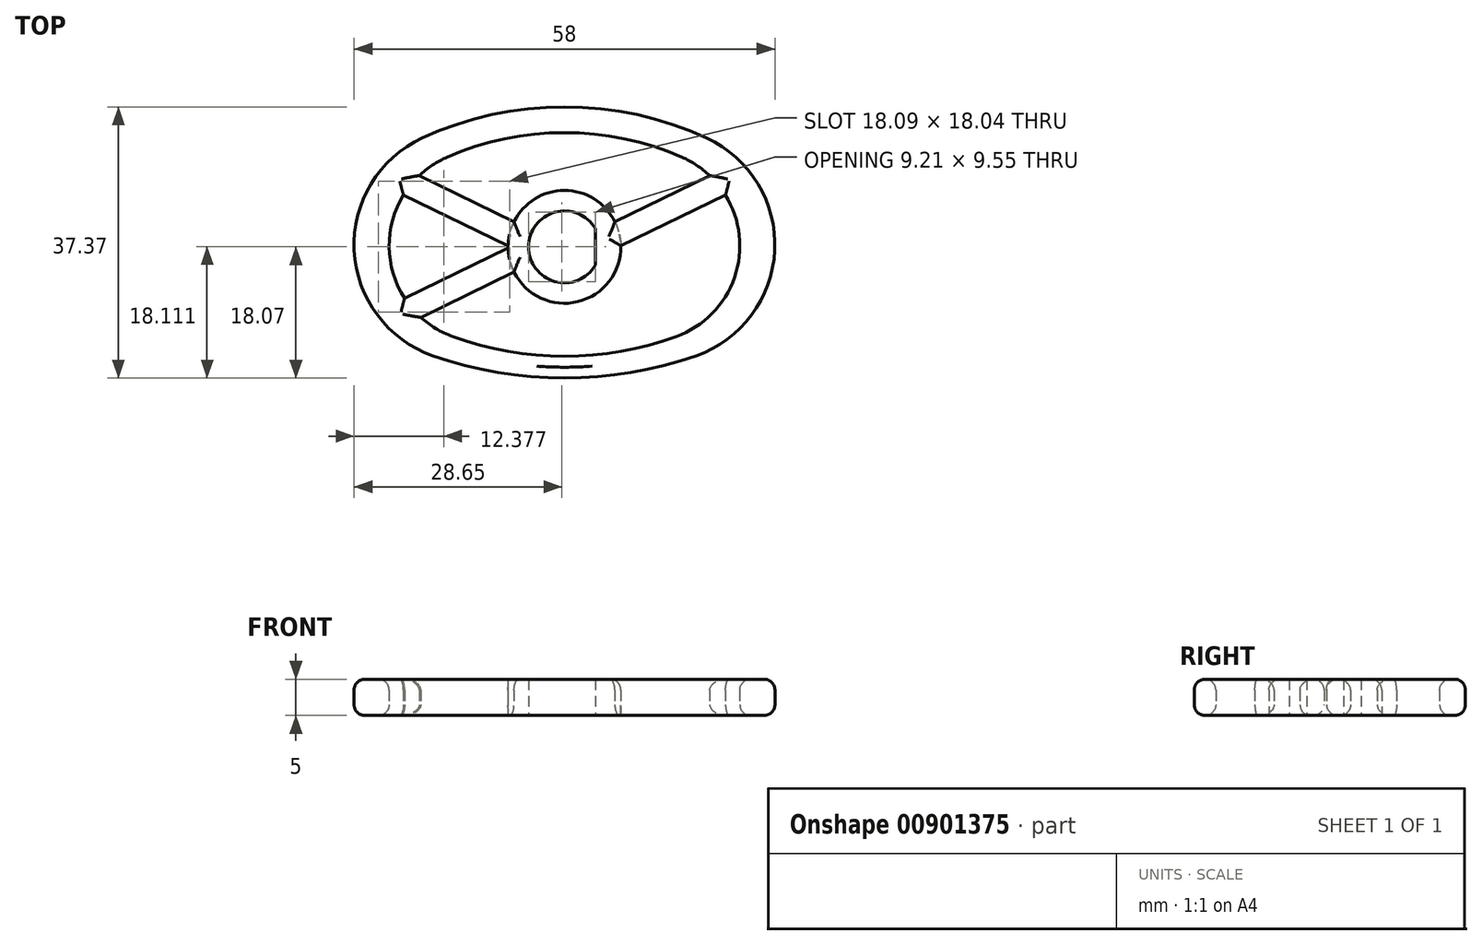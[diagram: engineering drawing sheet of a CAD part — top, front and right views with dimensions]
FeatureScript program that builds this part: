
annotation { "Feature Type Name" : "Feature", "Feature Type Description" : "" }
export const myFeature = defineFeature(function(context is Context, id is Id, definition is map)
    precondition{}
    {
        {
            var Q0;
            Q0=qCreatedBy(makeId("Top.planeOp"),FACE);
            var sketch = newSketch(context, id + "F0", { "sketchPlane" : qUnion([Q0])});
            skArc(sketch, "E0", {"start": v(4.25, 2.54) * mm, "mid": v(-4.95, 0) * mm, "end": v(4.25, -2.54) * mm});
            skLineSegment(sketch, "E1", {"start": v(4.25, 2.54) * mm, "end": v(4.25, -2.54) * mm});
            skArc(sketch, "E2", {"start": v(-19.59, 15) * mm, "mid": v(-28.98, -0.49) * mm, "end": v(-18.14, -15) * mm});
            skArc(sketch, "E3.MirrorCS", {"start": v(19.59, 15) * mm, "mid": v(28.98, -0.49) * mm, "end": v(18.14, -15) * mm});
            skArc(sketch, "E4", {"start": v(19.59, 15) * mm, "mid": v(0, 19.3) * mm, "end": v(-19.59, 15) * mm});
            skArc(sketch, "E5", {"start": v(-18.14, -15) * mm, "mid": v(0, -18.07) * mm, "end": v(18.14, -15) * mm});
            skArc(sketch, "E6", {"start": v(-16.17, 12.37) * mm, "mid": v(-24.16, -0.26) * mm, "end": v(-15.41, -12.37) * mm});
            skArc(sketch, "E7.MirrorCS", {"start": v(16.17, 12.37) * mm, "mid": v(24.16, -0.26) * mm, "end": v(15.41, -12.37) * mm});
            skArc(sketch, "E8", {"start": v(16.17, 12.37) * mm, "mid": v(0, 15.74) * mm, "end": v(-16.17, 12.37) * mm});
            skArc(sketch, "E9", {"start": v(-15.41, -12.37) * mm, "mid": v(0, -15.1) * mm, "end": v(15.41, -12.37) * mm});
            skCircle(sketch, "E10", {"center": v(0, 0) * mm, "radius": 7.77 * mm});
            skLineSegment(sketch, "E11", {"start": v(-7.77, 0.15) * mm, "end": v(-22.19, 7.15) * mm});
            skLineSegment(sketch, "E12", {"start": v(-6.95, 3.49) * mm, "end": v(-20.01, 9.83) * mm});
            skLineSegment(sketch, "E13.MirrorCS", {"start": v(6.95, 3.49) * mm, "end": v(20.01, 9.83) * mm});
            skLineSegment(sketch, "E14.MirrorCS", {"start": v(7.77, 0.15) * mm, "end": v(22.19, 7.15) * mm});
            skLineSegment(sketch, "E15.MirrorCS", {"start": v(-7.77, -0.15) * mm, "end": v(-22.19, -7.15) * mm});
            skLineSegment(sketch, "E16.MirrorCS", {"start": v(-6.95, -3.49) * mm, "end": v(-20.01, -9.83) * mm});
            skLineSegment(sketch, "E17.MirrorCS", {"start": v(7.77, -0.15) * mm, "end": v(22.19, -7.15) * mm});
            skLineSegment(sketch, "E18.MirrorCS", {"start": v(6.95, -3.49) * mm, "end": v(20.01, -9.83) * mm});
            skSolve(sketch);
        }
        {
            var Q0;
            Q0=makeQuery(id+"F0.imprint","IMPRINT",FACE,{"disambiguationData":[TD([[makeQuery(id+"F0.imprint","IMPRINT",EDGE,{"derivedFrom":sQuery(id+"F0.wireOp",EDGE,"E2")}),1.0]])]});
            var Q1;
            {var subQ0=sQuery(id+"F0.wireOp",EDGE,"38c7c2e5-10ad-45b0-9486-c35c668e693a0.MirrorCS");Q1=makeQuery(id+"F0.imprint","IMPRINT",FACE,{"disambiguationData":[TD([[makeQuery(id+"F0.imprint","IMPRINT",EDGE,{"derivedFrom":subQ0}),1.0]])]});}
            var Q2;
            {var subQ0=sQuery(id+"F0.wireOp",EDGE,"8eY9Tq4a-0Rdl-XbM1-Jlny-iYoXFbPFEpTW");Q2=makeQuery(id+"F0.imprint","IMPRINT",FACE,{"disambiguationData":[TD([[makeQuery(id+"F0.imprint","IMPRINT",EDGE,{"derivedFrom":subQ0}),-1.0]])]});}
            var Q3;
            Q3=makeQuery(id+"F0.imprint","IMPRINT",FACE,{"disambiguationData":[TD([[makeQuery(id+"F0.imprint","IMPRINT",EDGE,{"derivedFrom":sQuery(id+"F0.wireOp",EDGE,"E0")}),-1.0]])]});
            var Q4;
            {var subQ0=sQuery(id+"F0.wireOp",EDGE,"XcB9EYdE-zTz3-5Oig-SbUN-aXQNURDI4oZK");Q4=makeQuery(id+"F0.imprint","IMPRINT",FACE,{"disambiguationData":[TD([[makeQuery(id+"F0.imprint","IMPRINT",EDGE,{"derivedFrom":subQ0}),-1.0]])]});}
            var Q5;
            {var subQ0=sQuery(id+"F0.wireOp",EDGE,"E11");Q5=makeQuery(id+"F0.imprint","IMPRINT",FACE,{"disambiguationData":[TD([[makeQuery(id+"F0.imprint","IMPRINT",EDGE,{"derivedFrom":subQ0}),-1.0]])]});}
            var Q6;
            {var subQ0=sQuery(id+"F0.wireOp",EDGE,"E13.MirrorCS");Q6=makeQuery(id+"F0.imprint","IMPRINT",FACE,{"disambiguationData":[TD([[makeQuery(id+"F0.imprint","IMPRINT",EDGE,{"derivedFrom":subQ0}),-1.0]])]});}
            var Q7;
            {var subQ0=sQuery(id+"F0.wireOp",EDGE,"E17.MirrorCS");var subQ1=sQuery(id+"F0.wireOp",EDGE,"E7.MirrorCS");var subQ2=makeQuery(id+"F0.imprint","INTERSECT",VERTEX,{"derivedFrom":[subQ1,subQ0]});Q7=makeQuery(id+"F0.imprint","IMPRINT",FACE,{"disambiguationData":[TD([[makeQuery(id+"F0.imprint","IMPRINT",EDGE,{"disambiguationData":[TD([[subQ2,-1.0]])],"derivedFrom":subQ1}),-1.0]])]});}
            var Q8;
            {var subQ0=sQuery(id+"F0.wireOp",EDGE,"E15.MirrorCS");var subQ1=sQuery(id+"F0.wireOp",EDGE,"E6");var subQ2=makeQuery(id+"F0.imprint","INTERSECT",VERTEX,{"derivedFrom":[subQ1,subQ0]});Q8=makeQuery(id+"F0.imprint","IMPRINT",FACE,{"disambiguationData":[TD([[makeQuery(id+"F0.imprint","IMPRINT",EDGE,{"disambiguationData":[TD([[subQ2,-1.0]])],"derivedFrom":subQ1}),1.0]])]});}
            extrude(context, id + "F1", {"entities" : qUnion([Q0, Q1, Q2, Q3, Q4, Q5, Q6, Q7, Q8]), "depth" : 5 * mm, "offsetDistance" : 25.4 * mm});
        }
        {
            var Q0;
            Q0=makeQuery(id+"F1.opExtrude","CAP_EDGE",EDGE,{"disambiguationData":[OSD([sQuery(id+"F0.wireOp",EDGE,"E5")])],"isStart":false});
            var Q1;
            Q1=makeQuery(id+"F1.opExtrude","CAP_EDGE",EDGE,{"disambiguationData":[OSD([sQuery(id+"F0.wireOp",EDGE,"E5")])],"isStart":true});
            var Q2;
            {var subQ0=sQuery(id+"F0.wireOp",EDGE,"E7.MirrorCS");Q2=makeQuery(id+"F1.opExtrude","CAP_EDGE",EDGE,{"disambiguationData":[OSD([subQ0]),TDD([makeQuery(id+"F0.imprint","IMPRINT",EDGE,{"disambiguationData":[TD([[makeQuery(id+"F0.imprint","INTERSECT",VERTEX,{"derivedFrom":[subQ0,sQuery(id+"F0.wireOp",EDGE,"E14.MirrorCS")]}),-1.0]])],"derivedFrom":subQ0})])],"isStart":false});}
            var Q3;
            Q3=makeQuery(id+"F1.opExtrude","CAP_EDGE",EDGE,{"disambiguationData":[OSD([sQuery(id+"F0.wireOp",EDGE,"E8")])],"isStart":false});
            var Q4;
            {var subQ0=sQuery(id+"F0.wireOp",EDGE,"E6");Q4=makeQuery(id+"F1.opExtrude","CAP_EDGE",EDGE,{"disambiguationData":[OSD([subQ0]),TDD([makeQuery(id+"F0.imprint","IMPRINT",EDGE,{"disambiguationData":[TD([[makeQuery(id+"F0.imprint","INTERSECT",VERTEX,{"derivedFrom":[subQ0,sQuery(id+"F0.wireOp",EDGE,"E8")]}),-1.0]])],"derivedFrom":subQ0})])],"isStart":false});}
            var Q5;
            {var subQ0=sQuery(id+"F0.wireOp",EDGE,"E6");Q5=makeQuery(id+"F1.opExtrude","CAP_EDGE",EDGE,{"disambiguationData":[OSD([subQ0]),TDD([makeQuery(id+"F0.imprint","IMPRINT",EDGE,{"disambiguationData":[TD([[makeQuery(id+"F0.imprint","INTERSECT",VERTEX,{"derivedFrom":[subQ0,sQuery(id+"F0.wireOp",EDGE,"E11")]}),-1.0]])],"derivedFrom":subQ0})])],"isStart":false});}
            var Q6;
            Q6=makeQuery(id+"F1.opExtrude","CAP_EDGE",EDGE,{"disambiguationData":[OSD([sQuery(id+"F0.wireOp",EDGE,"E9")])],"isStart":false});
            var Q7;
            Q7=makeQuery(id+"F1.opExtrude","CAP_EDGE",EDGE,{"disambiguationData":[OSD([sQuery(id+"F0.wireOp",EDGE,"E18.MirrorCS")])],"isStart":false});
            var Q8;
            {var subQ0=sQuery(id+"F0.wireOp",EDGE,"E10");Q8=makeQuery(id+"F1.opExtrude","CAP_EDGE",EDGE,{"disambiguationData":[OSD([subQ0]),TDD([makeQuery(id+"F0.imprint","IMPRINT",EDGE,{"disambiguationData":[TD([[makeQuery(id+"F0.imprint","INTERSECT",VERTEX,{"derivedFrom":[subQ0,sQuery(id+"F0.wireOp",EDGE,"E16.MirrorCS")]}),-1.0]])],"derivedFrom":subQ0})])],"isStart":false});}
            var Q9;
            {var subQ0=sQuery(id+"F0.wireOp",EDGE,"E10");Q9=makeQuery(id+"F1.opExtrude","CAP_EDGE",EDGE,{"disambiguationData":[OSD([subQ0]),TDD([makeQuery(id+"F0.imprint","IMPRINT",EDGE,{"disambiguationData":[TD([[makeQuery(id+"F0.imprint","INTERSECT",VERTEX,{"derivedFrom":[subQ0,sQuery(id+"F0.wireOp",EDGE,"E12")]}),1.0]])],"derivedFrom":subQ0})])],"isStart":false});}
            var Q10;
            Q10=makeQuery(id+"F1.opExtrude","CAP_EDGE",EDGE,{"disambiguationData":[OSD([sQuery(id+"F0.wireOp",EDGE,"E14.MirrorCS")])],"isStart":false});
            var Q11;
            Q11=makeQuery(id+"F1.opExtrude","CAP_EDGE",EDGE,{"disambiguationData":[OSD([sQuery(id+"F0.wireOp",EDGE,"E16.MirrorCS")])],"isStart":false});
            var Q12;
            Q12=makeQuery(id+"F1.opExtrude","CAP_EDGE",EDGE,{"disambiguationData":[OSD([sQuery(id+"F0.wireOp",EDGE,"E15.MirrorCS")])],"isStart":false});
            var Q13;
            Q13=makeQuery(id+"F1.opExtrude","CAP_EDGE",EDGE,{"disambiguationData":[OSD([sQuery(id+"F0.wireOp",EDGE,"E17.MirrorCS")])],"isStart":false});
            var Q14;
            Q14=makeQuery(id+"F1.opExtrude","CAP_EDGE",EDGE,{"disambiguationData":[OSD([sQuery(id+"F0.wireOp",EDGE,"E11")])],"isStart":false});
            var Q15;
            Q15=makeQuery(id+"F1.opExtrude","CAP_EDGE",EDGE,{"disambiguationData":[OSD([sQuery(id+"F0.wireOp",EDGE,"E12")])],"isStart":false});
            var Q16;
            Q16=makeQuery(id+"F1.opExtrude","CAP_EDGE",EDGE,{"disambiguationData":[OSD([sQuery(id+"F0.wireOp",EDGE,"E13.MirrorCS")])],"isStart":false});
            var Q17;
            Q17=makeQuery(id+"F1.opExtrude","CAP_EDGE",EDGE,{"disambiguationData":[OSD([sQuery(id+"F0.wireOp",EDGE,"E16.MirrorCS")])],"isStart":true});
            var Q18;
            Q18=makeQuery(id+"F1.opExtrude","CAP_EDGE",EDGE,{"disambiguationData":[OSD([sQuery(id+"F0.wireOp",EDGE,"E11")])],"isStart":true});
            var Q19;
            {var subQ0=sQuery(id+"F0.wireOp",EDGE,"E6");Q19=makeQuery(id+"F1.opExtrude","CAP_EDGE",EDGE,{"disambiguationData":[OSD([subQ0]),TDD([makeQuery(id+"F0.imprint","IMPRINT",EDGE,{"disambiguationData":[TD([[makeQuery(id+"F0.imprint","INTERSECT",VERTEX,{"derivedFrom":[subQ0,sQuery(id+"F0.wireOp",EDGE,"E11")]}),-1.0]])],"derivedFrom":subQ0})])],"isStart":true});}
            var Q20;
            Q20=makeQuery(id+"F1.opExtrude","CAP_EDGE",EDGE,{"disambiguationData":[OSD([sQuery(id+"F0.wireOp",EDGE,"E8")])],"isStart":true});
            var Q21;
            {var subQ0=sQuery(id+"F0.wireOp",EDGE,"E7.MirrorCS");Q21=makeQuery(id+"F1.opExtrude","CAP_EDGE",EDGE,{"disambiguationData":[OSD([subQ0]),TDD([makeQuery(id+"F0.imprint","IMPRINT",EDGE,{"disambiguationData":[TD([[makeQuery(id+"F0.imprint","INTERSECT",VERTEX,{"derivedFrom":[subQ0,sQuery(id+"F0.wireOp",EDGE,"E14.MirrorCS")]}),-1.0]])],"derivedFrom":subQ0})])],"isStart":true});}
            var Q22;
            Q22=makeQuery(id+"F1.opExtrude","CAP_EDGE",EDGE,{"disambiguationData":[OSD([sQuery(id+"F0.wireOp",EDGE,"E9")])],"isStart":true});
            var Q23;
            Q23=makeQuery(id+"F1.opExtrude","CAP_EDGE",EDGE,{"disambiguationData":[OSD([sQuery(id+"F0.wireOp",EDGE,"E18.MirrorCS")])],"isStart":true});
            var Q24;
            Q24=makeQuery(id+"F1.opExtrude","CAP_EDGE",EDGE,{"disambiguationData":[OSD([sQuery(id+"F0.wireOp",EDGE,"E14.MirrorCS")])],"isStart":true});
            var Q25;
            Q25=makeQuery(id+"F1.opExtrude","CAP_EDGE",EDGE,{"disambiguationData":[OSD([sQuery(id+"F0.wireOp",EDGE,"E13.MirrorCS")])],"isStart":true});
            var Q26;
            Q26=makeQuery(id+"F1.opExtrude","CAP_EDGE",EDGE,{"disambiguationData":[OSD([sQuery(id+"F0.wireOp",EDGE,"E15.MirrorCS")])],"isStart":true});
            var Q27;
            Q27=makeQuery(id+"F1.opExtrude","CAP_EDGE",EDGE,{"disambiguationData":[OSD([sQuery(id+"F0.wireOp",EDGE,"E12")])],"isStart":true});
            var Q28;
            Q28=makeQuery(id+"F1.opExtrude","CAP_EDGE",EDGE,{"disambiguationData":[OSD([sQuery(id+"F0.wireOp",EDGE,"E17.MirrorCS")])],"isStart":true});
            fillet(context, id + "F2", {"entities" : qUnion([Q0, Q1, Q2, Q3, Q4, Q5, Q6, Q7, Q8, Q9, Q10, Q11, Q12, Q13, Q14, Q15, Q16, Q17, Q18, Q19, Q20, Q21, Q22, Q23, Q24, Q25, Q26, Q27, Q28]), "radius" : 1.5 * mm, "tangentPropagation" : true, "allowEdgeOverflow" : false});
        }
    });
